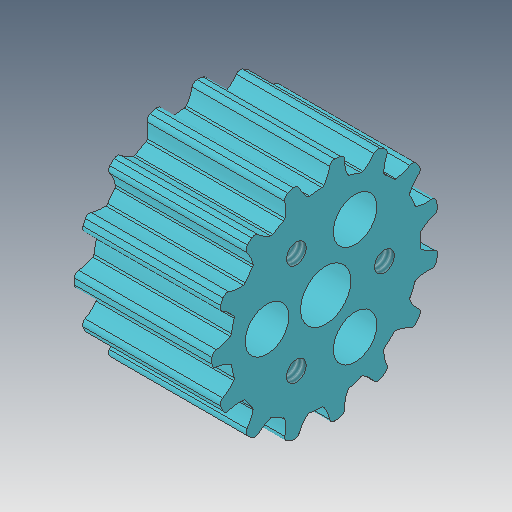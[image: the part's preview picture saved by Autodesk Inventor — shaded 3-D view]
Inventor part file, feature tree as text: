
AUTODESK INVENTOR PART (.ipt)
format: ipt  version: 2019.4 (Build 234330000, 330)  size: 280,064 bytes
history: native  units: mm
features: sketch x4, hole x3, fillet x2, other x1, extrude x1, pattern_circular x1
ambient origin geometry x8: Origin, YZ Plane, XZ Plane, XY Plane, X Axis, Y Axis, Z Axis, Center Point
bodies: Body1 (feature_tree)
feature tree (12):
  other  "ソリッド1"
  extrude  "押し出し1"  Depth=1.95mm
  fillet  "フィレット1"  Radius=1.975mm
  fillet  "フィレット2"  Radius=1.11mm
  pattern_circular  "円形状パターン1"  [2 undecoded]
  hole  "穴1"  [1 undecoded]
  sketch  "スケッチ3"
  hole  "穴2"  [1 undecoded]
  hole  "穴3"  [1 undecoded]
  sketch  "スケッチ4"
  sketch  "スケッチ1"
  sketch  "スケッチ2"
note: 5 required parameter values undecoded (feature->parameter linkage not recoverable at this tier; creation-order binding heuristic only, values carry confidence <= 0.55)
